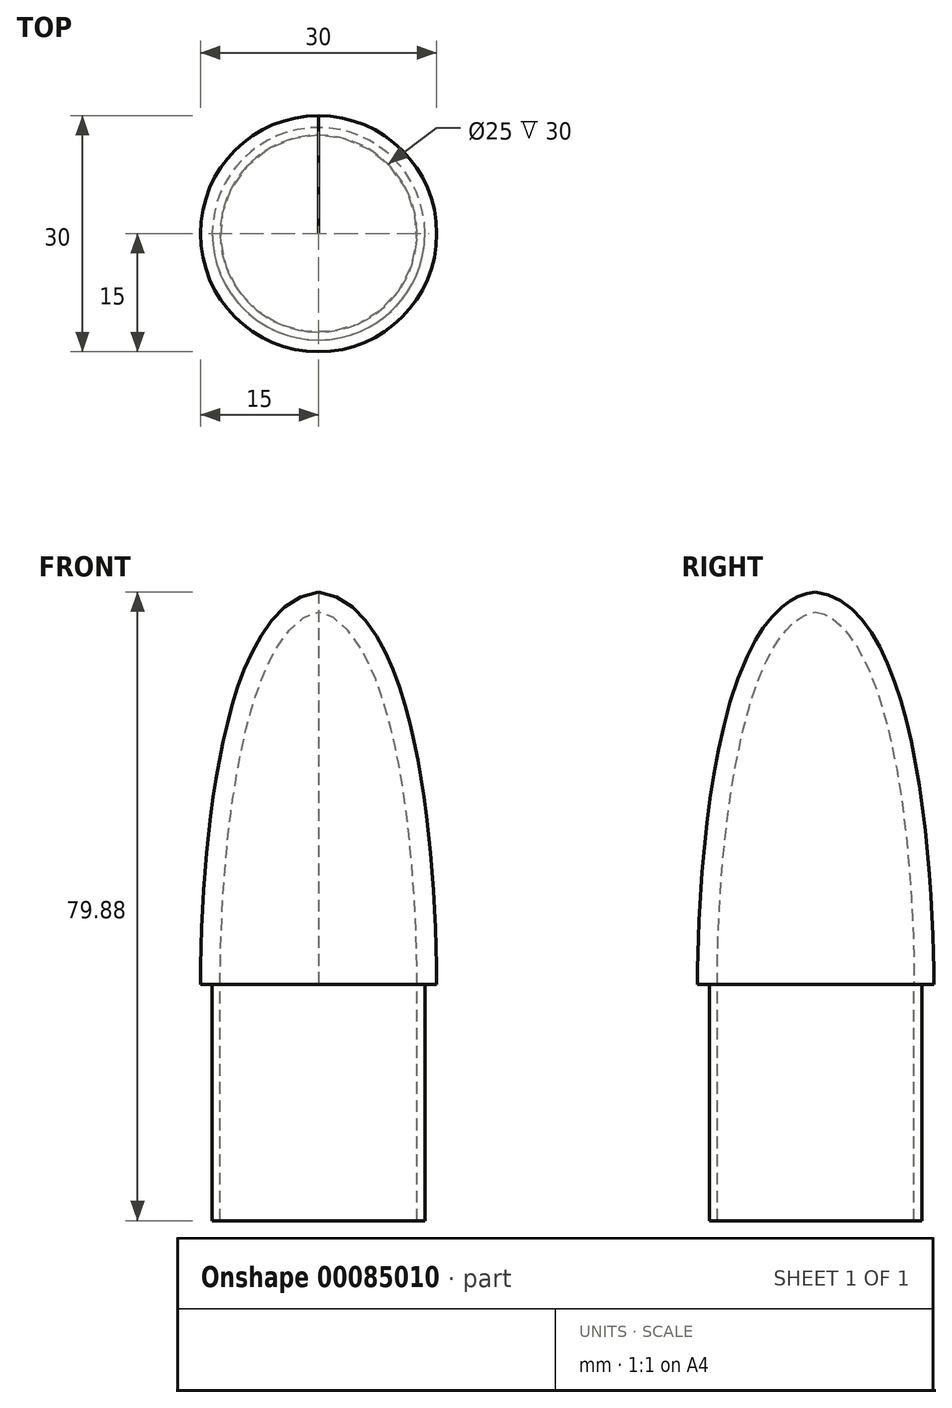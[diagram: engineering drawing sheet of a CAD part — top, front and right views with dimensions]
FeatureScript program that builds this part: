
annotation { "Feature Type Name" : "Feature", "Feature Type Description" : "" }
export const myFeature = defineFeature(function(context is Context, id is Id, definition is map)
    precondition{}
    {
        {
            var Q0;
            Q0=qCreatedBy(makeId("Right.planeOp"),FACE);
            var sketch = newSketch(context, id + "F0", { "sketchPlane" : qUnion([Q0])});
            skLineSegment(sketch, "E0.bottom", {"start": v(-15, 25) * mm, "end": v(15, 25) * mm});
            skLineSegment(sketch, "E0.top", {"start": v(-15, -25) * mm, "end": v(15, -25) * mm});
            skLineSegment(sketch, "E0.left", {"start": v(-15, 25) * mm, "end": v(-15, -25) * mm});
            skLineSegment(sketch, "E0.right", {"start": v(15, 25) * mm, "end": v(15, -25) * mm});
            skPoint(sketch, "E0.middle", {"position": v(0, 0) * mm});
            skPoint(sketch, "E1", {"position": v(0, 25) * mm});
            skFitSpline(sketch, "E2", {"points": [v(0, 25) * mm, v(-15, -25) * mm], "startDerivative": vector(-37.66, 0) * mm, "endDerivative": vector(0, -43.96) * mm});
            skFitSpline(sketch, "E3", {"points": [v(-0.96, 24.93) * mm, v(15, -25) * mm], "startDerivative": vector(42, 0.21) * mm, "endDerivative": vector(0, -41.9) * mm});
            skLineSegment(sketch, "E4", {"start": v(0, 25) * mm, "end": v(0, -25) * mm, "construction": true});
            skLineSegment(sketch, "E5", {"start": v(0, 25) * mm, "end": v(0, -25) * mm});
            skSolve(sketch);
        }
        {
            var Q0;
            {var subQ1=sQuery(id+"F0.wireOp",EDGE,"E0.top");var subQ3=sQuery(id+"F0.wireOp",EDGE,"E5");var subQ4=makeQuery(id+"F0.imprint","INTERSECT",VERTEX,{"derivedFrom":[subQ1,subQ3]});Q0=makeQuery(id+"F0.imprint","IMPRINT",FACE,{"disambiguationData":[TD([[makeQuery(id+"F0.imprint","IMPRINT",EDGE,{"disambiguationData":[TD([[subQ4,1.0]])],"derivedFrom":subQ3}),1.0]])]});}
            var Q1;
            Q1=sQuery(id+"F0.wireOp",EDGE,"E5");
            revolve(context, id + "F1", {"entities" : qUnion([Q0]), "axis" : qUnion([Q1]), "revolveType" : RevolveType.FULL});
        }
        {
            var Q0;
            Q0=makeQuery(id+"F1.opRevolve","SWEPT_FACE",FACE,{"disambiguationData":[OSD([sQuery(id+"F0.wireOp",EDGE,"E0.top")])]});
            shell(context, id + "F2", {"entities" : qUnion([Q0]), "thickness" : 2.5 * mm});
        }
        {
            var Q0;
            Q0=makeQuery(id+"F1.opRevolve","SWEPT_FACE",FACE,{"disambiguationData":[OSD([sQuery(id+"F0.wireOp",EDGE,"E0.top")])]});
            var sketch = newSketch(context, id + "F3", { "sketchPlane" : qUnion([Q0])});
            skCircle(sketch, "E6", {"center": v(0, 0) * mm, "radius": 12.5 * mm});
            skCircle(sketch, "E7", {"center": v(0, 0) * mm, "radius": 13.5 * mm});
            skSolve(sketch);
        }
        {
            var Q0;
            Q0=qSketchRegion(id+"F3",true);
            extrude(context, id + "F4", {"entities" : qUnion([Q0]), "operationType" : NewBodyOperationType.ADD, "depth" : 30 * mm});
        }
    });
